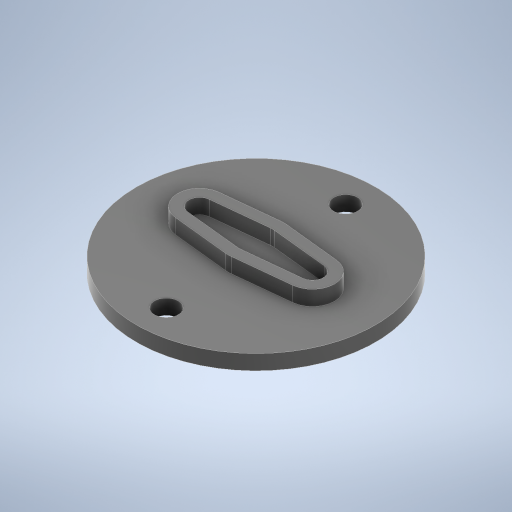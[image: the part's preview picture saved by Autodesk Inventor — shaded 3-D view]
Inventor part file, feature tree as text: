
AUTODESK INVENTOR PART (.ipt)
format: ipt  version: 2024 (Build 280153000, 153)  size: 288,256 bytes
history: native  units: in
note: dims shown in document units (in); Inventor stores cm internally (conversion verified against a paired STEP export)
features: extrude x2, sketch x2
ambient origin geometry x8: Origin, YZ Plane, XZ Plane, XY Plane, X Axis, Y Axis, Z Axis, Center Point
bodies: Solid1 (feature_tree)
feature tree (4):
  extrude  "Extrusion1"  Depth=0.2in
  extrude  "Extrusion2"  Depth=0.125in
  sketch  "Sketch1"  dims[d0=2.0in d1=0.2in]
  sketch  "Sketch2"  dims[d2=0.2in d3=1.5in d4=0.125in d5=0.0in d6=0.2165in d7=0.1181in d8=1.063in d9=0.0312in d10=0.0312in d11=0.0312in d12=0.0312in d13=0.0312in d14=0.0312in d15=0.0312in d16=0.0938in d17=0.0938in d18=0.0938in d19=0.0938in d20=0.0938in d21=0.0938in d22=0.0938in d23=0.125in d24=0.0in]
